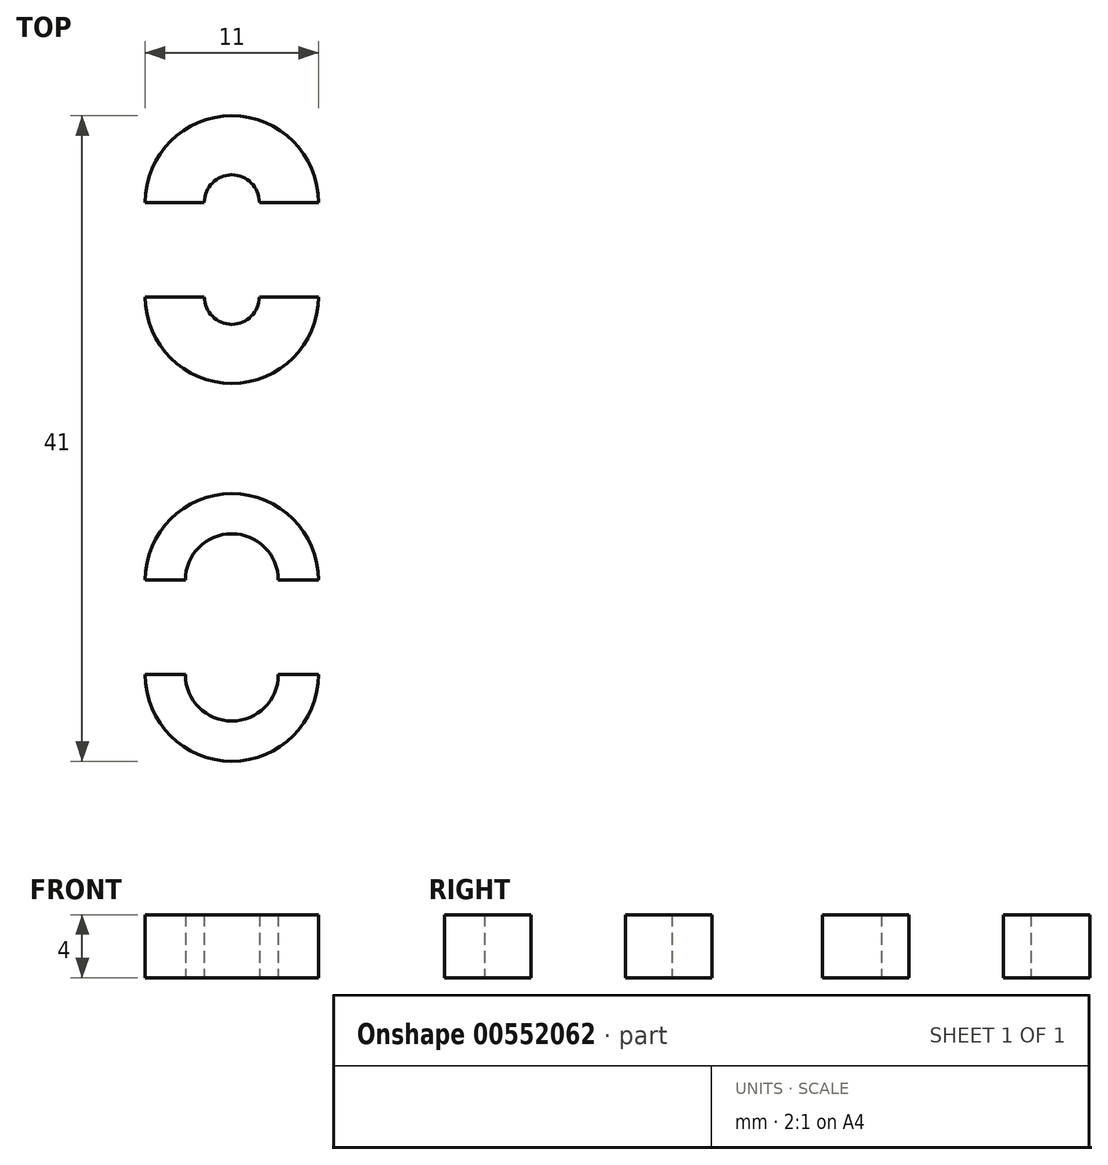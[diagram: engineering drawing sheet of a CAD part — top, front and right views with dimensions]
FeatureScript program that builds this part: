
annotation { "Feature Type Name" : "Feature", "Feature Type Description" : "" }
export const myFeature = defineFeature(function(context is Context, id is Id, definition is map)
    precondition{}
    {
        {
            var Q0;
            Q0=qCreatedBy(makeId("Top.planeOp"),FACE);
            var sketch = newSketch(context, id + "F0", { "sketchPlane" : qUnion([Q0])});
            skArc(sketch, "E0", {"start": v(5.5, 15) * mm, "mid": v(0, 20.5) * mm, "end": v(-5.5, 15) * mm});
            skArc(sketch, "E1", {"start": v(-5.5, -15) * mm, "mid": v(0, -20.5) * mm, "end": v(5.5, -15) * mm});
            skArc(sketch, "E2", {"start": v(1.75, 15) * mm, "mid": v(0, 16.75) * mm, "end": v(-1.75, 15) * mm});
            skArc(sketch, "E3", {"start": v(-2.95, -15) * mm, "mid": v(0, -17.95) * mm, "end": v(2.95, -15) * mm});
            skLineSegment(sketch, "E4", {"start": v(-5.5, -15) * mm, "end": v(-2.95, -15) * mm});
            skLineSegment(sketch, "E5", {"start": v(-5.5, 15) * mm, "end": v(-1.75, 15) * mm});
            skLineSegment(sketch, "E6.trimOffspring", {"start": v(1.75, 15) * mm, "end": v(5.5, 15) * mm});
            skLineSegment(sketch, "E7.trimOffspring", {"start": v(2.95, -15) * mm, "end": v(5.5, -15) * mm});
            skLineSegment(sketch, "E8", {"start": v(-8.57, 12) * mm, "end": v(8.33, 12) * mm});
            skLineSegment(sketch, "E9.MirrorCS", {"start": v(-8.57, -12) * mm, "end": v(8.33, -12) * mm});
            skArc(sketch, "E10.MirrorCS", {"start": v(1.75, 9) * mm, "mid": v(0, 7.25) * mm, "end": v(-1.75, 9) * mm});
            skArc(sketch, "E11.MirrorCS", {"start": v(5.5, 9) * mm, "mid": v(0, 3.5) * mm, "end": v(-5.5, 9) * mm});
            skLineSegment(sketch, "E12.MirrorCS", {"start": v(-5.5, 9) * mm, "end": v(-1.75, 9) * mm});
            skLineSegment(sketch, "E13.MirrorCS", {"start": v(1.75, 9) * mm, "end": v(5.5, 9) * mm});
            skLineSegment(sketch, "E14.MirrorCS", {"start": v(2.95, -9) * mm, "end": v(5.5, -9) * mm});
            skArc(sketch, "E15.MirrorCS", {"start": v(-5.5, -9) * mm, "mid": v(0, -3.5) * mm, "end": v(5.5, -9) * mm});
            skArc(sketch, "E16.MirrorCS", {"start": v(-2.95, -9) * mm, "mid": v(0, -6.05) * mm, "end": v(2.95, -9) * mm});
            skLineSegment(sketch, "E17.MirrorCS", {"start": v(-5.5, -9) * mm, "end": v(-2.95, -9) * mm});
            skSolve(sketch);
        }
        {
            var Q0;
            Q0 = qSketchRegion(id + "F0", true);
            extrude(context, id + "F1", {"entities" : qUnion([Q0]), "depth" : 4 * mm, "offsetDistance" : 25 * mm});
        }
    });
